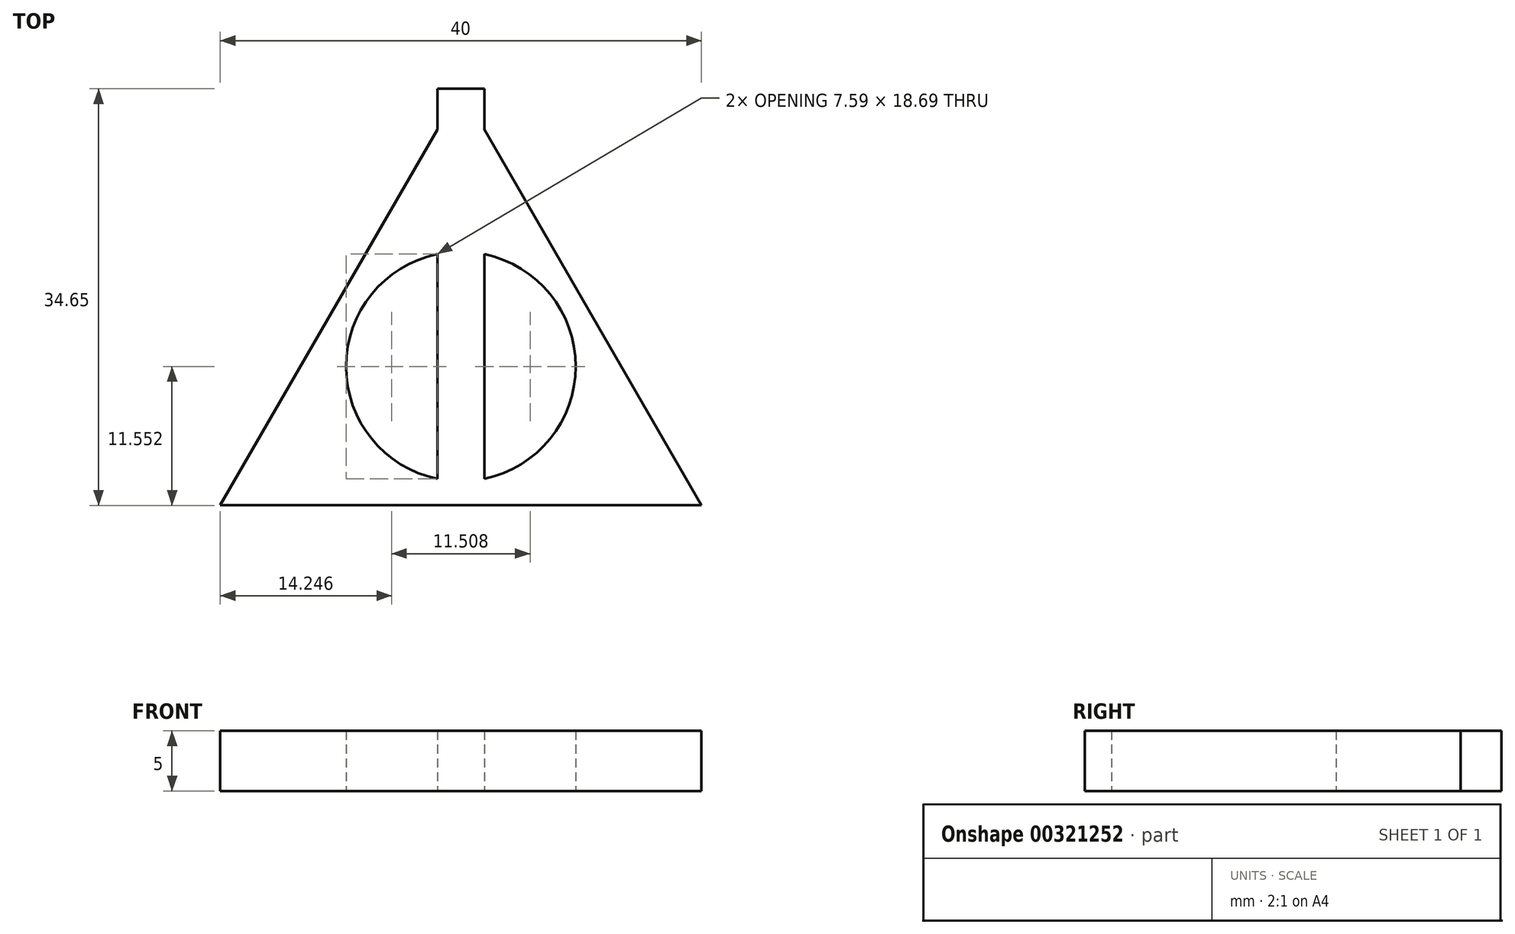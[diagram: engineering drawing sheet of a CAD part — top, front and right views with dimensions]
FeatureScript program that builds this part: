
annotation { "Feature Type Name" : "Feature", "Feature Type Description" : "" }
export const myFeature = defineFeature(function(context is Context, id is Id, definition is map)
    precondition{}
    {
        {
            var Q0;
            Q0=qCreatedBy(makeId("Top.planeOp"),FACE);
            var sketch = newSketch(context, id + "F0", { "sketchPlane" : qUnion([Q0])});
            skLineSegment(sketch, "E0", {"start": v(-1.96, 20.32) * mm, "end": v(-20, -10.93) * mm});
            skLineSegment(sketch, "E1.MirrorCS", {"start": v(1.96, 20.32) * mm, "end": v(20, -10.93) * mm});
            skLineSegment(sketch, "E2", {"start": v(-20, -10.93) * mm, "end": v(20, -10.93) * mm});
            skArc(sketch, "E3", {"start": v(-1.96, 12) * mm, "mid": v(0, -10.93) * mm, "end": v(1.96, 12) * mm});
            skPoint(sketch, "E3.first.point", {"position": v(-10, 6.4) * mm});
            skPoint(sketch, "E3.second.point", {"position": v(0, -10.93) * mm});
            skPoint(sketch, "E3.third.point", {"position": v(10, 6.4) * mm});
            skArc(sketch, "E4", {"start": v(-1.96, 9.97) * mm, "mid": v(-9.55, 0.62) * mm, "end": v(-1.96, -8.72) * mm});
            skLineSegment(sketch, "E5", {"start": v(-10, 6.4) * mm, "end": v(10, 6.4) * mm, "construction": true});
            skLineSegment(sketch, "E6.bottom", {"start": v(1.96, -10.93) * mm, "end": v(-1.96, -10.93) * mm});
            skLineSegment(sketch, "E6.top", {"start": v(1.96, 23.72) * mm, "end": v(-1.96, 23.72) * mm});
            skLineSegment(sketch, "E6.left", {"start": v(1.96, -10.93) * mm, "end": v(1.96, 12) * mm});
            skLineSegment(sketch, "E6.right", {"start": v(-1.96, -10.93) * mm, "end": v(-1.96, 12) * mm});
            skPoint(sketch, "E6.middle", {"position": v(0, 6.4) * mm});
            skArc(sketch, "E7.trimOffspring", {"start": v(1.96, -8.72) * mm, "mid": v(9.55, 0.62) * mm, "end": v(1.96, 9.97) * mm});
            skLineSegment(sketch, "E8.trimOffspring", {"start": v(1.96, 20.32) * mm, "end": v(1.96, 23.72) * mm});
            skLineSegment(sketch, "E9.trimOffspring", {"start": v(-1.96, 20.32) * mm, "end": v(-1.96, 23.72) * mm});
            skPoint(sketch, "E10.orphan", {"position": v(0, 23.72) * mm});
            skSolve(sketch);
        }
        {
            var Q0;
            Q0 = qSketchRegion(id + "F0", true);
            extrude(context, id + "F1", {"entities" : qUnion([Q0]), "depth" : 5 * mm});
        }
    });
